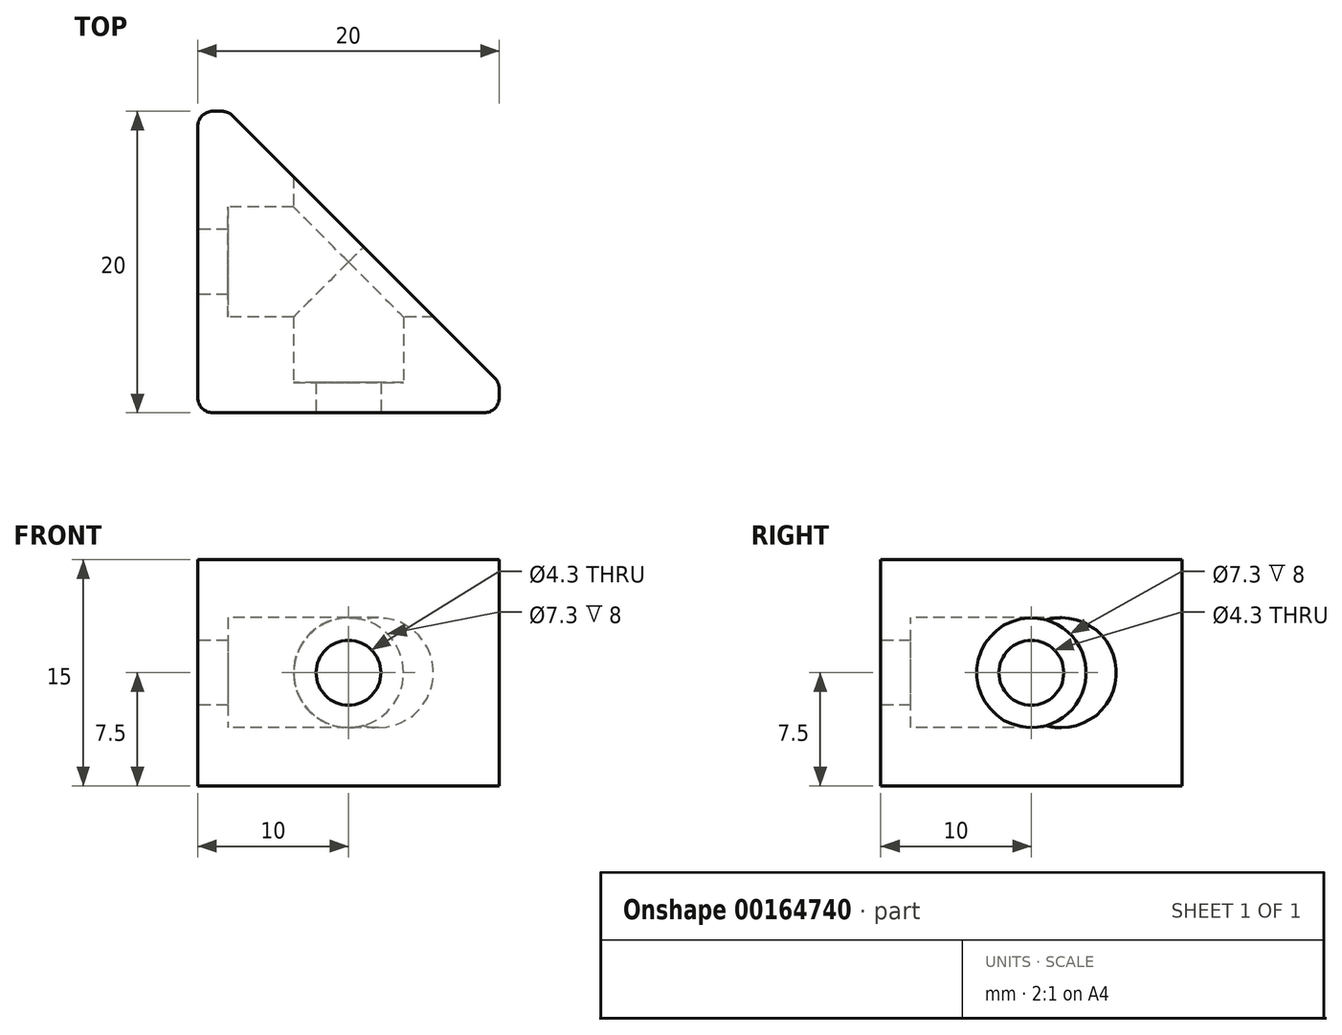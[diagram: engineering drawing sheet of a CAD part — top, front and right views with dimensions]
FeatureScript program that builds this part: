
annotation { "Feature Type Name" : "Feature", "Feature Type Description" : "" }
export const myFeature = defineFeature(function(context is Context, id is Id, definition is map)
    precondition{}
    {
        {
            var Q0;
            Q0=qCreatedBy(makeId("Top.planeOp"),FACE);
            var sketch = newSketch(context, id + "F0", { "sketchPlane" : qUnion([Q0])});
            skLineSegment(sketch, "E0", {"start": v(0, 0) * mm, "end": v(20, 0) * mm});
            skLineSegment(sketch, "E1", {"start": v(20, 0) * mm, "end": v(20, 2) * mm});
            skLineSegment(sketch, "E2", {"start": v(20, 2) * mm, "end": v(2, 20) * mm});
            skLineSegment(sketch, "E3", {"start": v(2, 20) * mm, "end": v(0, 20) * mm});
            skLineSegment(sketch, "E4", {"start": v(0, 20) * mm, "end": v(0, 0) * mm});
            skSolve(sketch);
        }
        {
            var Q0;
            Q0=makeQuery(id+"F0.imprint","IMPRINT",FACE,{"disambiguationData":[TD([[makeQuery(id+"F0.imprint","IMPRINT",EDGE,{"derivedFrom":sQuery(id+"F0.wireOp",EDGE,"E0")}),1.0]])]});
            extrude(context, id + "F1", {"entities" : qUnion([Q0]), "endBound" : BoundingType.SYMMETRIC, "depth" : 15 * mm});
        }
        {
            var Q0;
            Q0=makeQuery(id+"F1.opExtrude","SWEPT_FACE",FACE,{"disambiguationData":[OSD([sQuery(id+"F0.wireOp",EDGE,"E4")])]});
            var sketch = newSketch(context, id + "F2", { "sketchPlane" : qUnion([Q0])});
            skCircle(sketch, "E5", {"center": v(-10, 0) * mm, "radius": 3.65 * mm});
            skCircle(sketch, "E6", {"center": v(-10, 0) * mm, "radius": 2.15 * mm});
            skSolve(sketch);
        }
        {
            var Q0;
            Q0=makeQuery(id+"F1.opExtrude","SWEPT_FACE",FACE,{"disambiguationData":[OSD([sQuery(id+"F0.wireOp",EDGE,"E0")])]});
            var sketch = newSketch(context, id + "F3", { "sketchPlane" : qUnion([Q0])});
            skCircle(sketch, "E7", {"center": v(10, 0) * mm, "radius": 2.15 * mm});
            skCircle(sketch, "E8", {"center": v(10, 0) * mm, "radius": 3.65 * mm});
            skSolve(sketch);
        }
        {
            var Q0;
            Q0=makeQuery(id+"F3.imprint","IMPRINT",FACE,{"disambiguationData":[TD([[makeQuery(id+"F3.imprint","IMPRINT",EDGE,{"derivedFrom":sQuery(id+"F3.wireOp",EDGE,"E7")}),1.0]])]});
            extrude(context, id + "F4", {"entities" : qUnion([Q0]), "operationType" : NewBodyOperationType.REMOVE, "oppositeDirection" : true, "depth" : 20 * mm});
        }
        {
            var Q0;
            Q0=makeQuery(id+"F2.imprint","IMPRINT",FACE,{"disambiguationData":[TD([[makeQuery(id+"F2.imprint","IMPRINT",EDGE,{"derivedFrom":sQuery(id+"F2.wireOp",EDGE,"E6")}),1.0]])]});
            extrude(context, id + "F5", {"entities" : qUnion([Q0]), "operationType" : NewBodyOperationType.REMOVE, "oppositeDirection" : true, "depth" : 20 * mm});
        }
        {
            var Q0;
            Q0=makeQuery(id+"F2.imprint","IMPRINT",FACE,{"disambiguationData":[TD([[makeQuery(id+"F2.imprint","IMPRINT",EDGE,{"derivedFrom":sQuery(id+"F2.wireOp",EDGE,"E5")}),1.0]])]});
            extrude(context, id + "F6", {"entities" : qUnion([Q0]), "operationType" : NewBodyOperationType.REMOVE, "oppositeDirection" : true, "depth" : 20 * mm, "hasSecondDirection" : true, "secondDirectionOppositeDirection" : true, "secondDirectionDepth" : 2 * mm});
        }
        {
            var Q0;
            Q0=makeQuery(id+"F3.imprint","IMPRINT",FACE,{"disambiguationData":[TD([[makeQuery(id+"F3.imprint","IMPRINT",EDGE,{"derivedFrom":sQuery(id+"F3.wireOp",EDGE,"E7")}),-1.0]])]});
            extrude(context, id + "F7", {"entities" : qUnion([Q0]), "operationType" : NewBodyOperationType.REMOVE, "oppositeDirection" : true, "depth" : 20 * mm, "hasSecondDirection" : true, "secondDirectionOppositeDirection" : true, "secondDirectionDepth" : 2 * mm});
        }
        {
            var Q0;
            Q0=makeQuery(id+"F1.opExtrude","SWEPT_EDGE",EDGE,{"disambiguationData":[OSD([sQuery(id+"F0.wireOp",EDGE,"E0"),sQuery(id+"F0.wireOp",EDGE,"E4")])]});
            var Q1;
            Q1=makeQuery(id+"F1.opExtrude","SWEPT_EDGE",EDGE,{"disambiguationData":[OSD([sQuery(id+"F0.wireOp",EDGE,"E0"),sQuery(id+"F0.wireOp",EDGE,"E1")])]});
            var Q2;
            Q2=makeQuery(id+"F1.opExtrude","SWEPT_EDGE",EDGE,{"disambiguationData":[OSD([sQuery(id+"F0.wireOp",EDGE,"E1"),sQuery(id+"F0.wireOp",EDGE,"E2")])]});
            var Q3;
            Q3=makeQuery(id+"F1.opExtrude","SWEPT_EDGE",EDGE,{"disambiguationData":[OSD([sQuery(id+"F0.wireOp",EDGE,"E2"),sQuery(id+"F0.wireOp",EDGE,"E3")])]});
            var Q4;
            Q4=makeQuery(id+"F1.opExtrude","SWEPT_EDGE",EDGE,{"disambiguationData":[OSD([sQuery(id+"F0.wireOp",EDGE,"E3"),sQuery(id+"F0.wireOp",EDGE,"E4")])]});
            fillet(context, id + "F8", {"entities" : qUnion([Q0, Q1, Q2, Q3, Q4]), "radius" : 1 * mm, "tangentPropagation" : true, "allowEdgeOverflow" : false});
        }
    });
